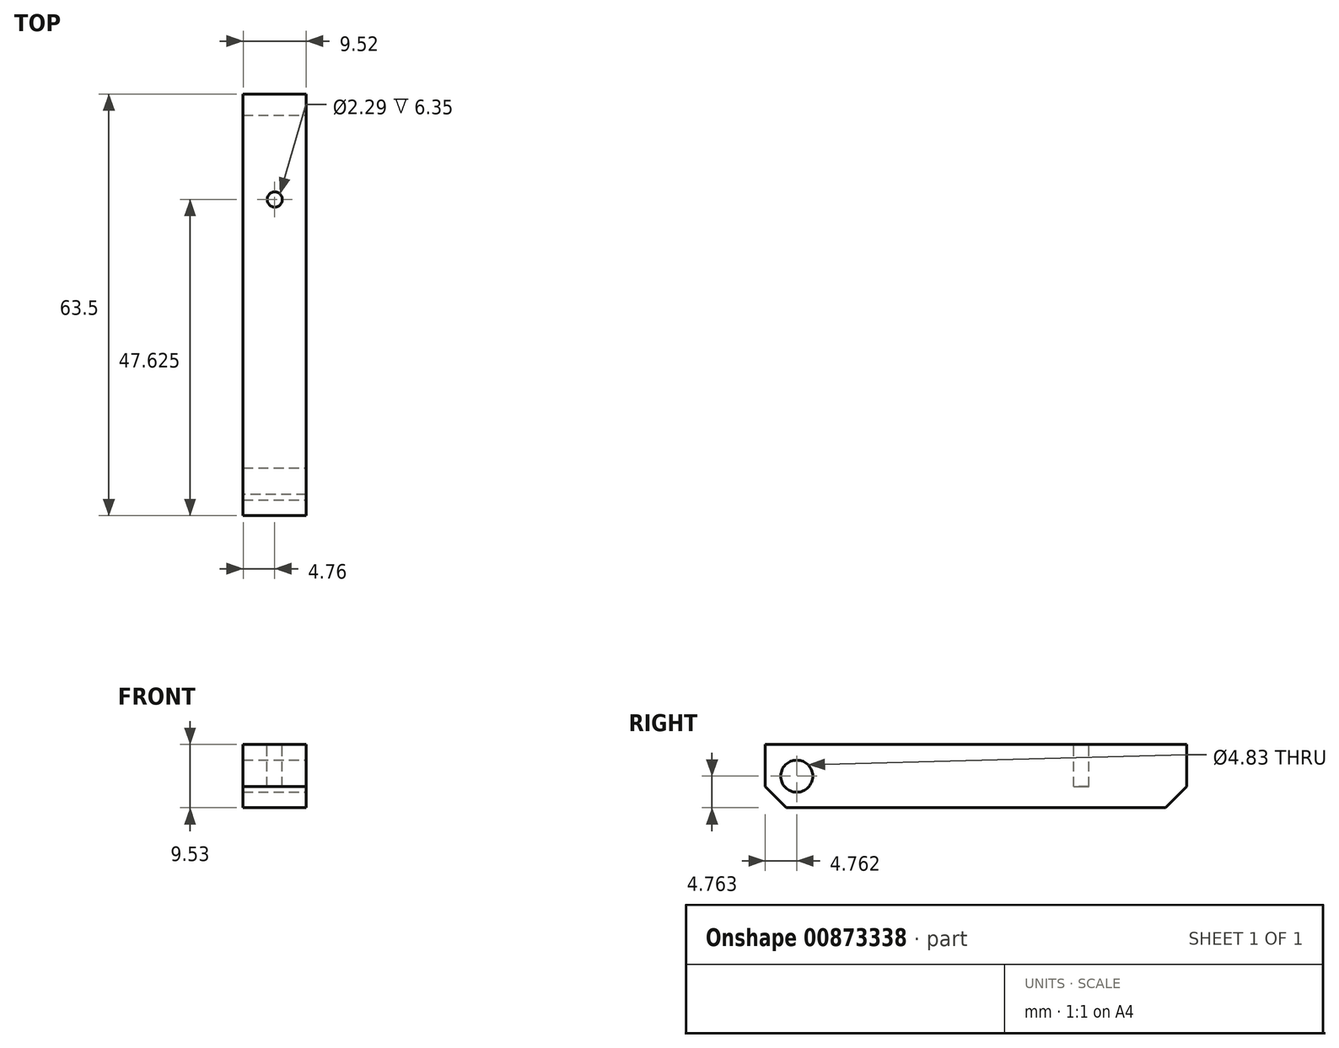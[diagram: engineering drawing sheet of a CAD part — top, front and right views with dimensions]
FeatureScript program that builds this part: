
annotation { "Feature Type Name" : "Feature", "Feature Type Description" : "" }
export const myFeature = defineFeature(function(context is Context, id is Id, definition is map)
    precondition{}
    {
        {
            var Q0;
            Q0=qCreatedBy(makeId("Top.planeOp"),FACE);
            var sketch = newSketch(context, id + "F0", { "sketchPlane" : qUnion([Q0])});
            skLineSegment(sketch, "E0.bottom", {"start": v(4.76, 31.75) * mm, "end": v(-4.76, 31.75) * mm});
            skLineSegment(sketch, "E0.top", {"start": v(4.76, -31.75) * mm, "end": v(-4.76, -31.75) * mm});
            skLineSegment(sketch, "E0.left", {"start": v(4.76, 31.75) * mm, "end": v(4.76, -31.75) * mm});
            skLineSegment(sketch, "E0.right", {"start": v(-4.76, 31.75) * mm, "end": v(-4.76, -31.75) * mm});
            skPoint(sketch, "E0.middle", {"position": v(0, 0) * mm});
            skSolve(sketch);
        }
        {
            var Q0;
            Q0=makeQuery(id+"F0.imprint","IMPRINT",FACE,{"disambiguationData":[TD([[makeQuery(id+"F0.imprint","IMPRINT",EDGE,{"derivedFrom":sQuery(id+"F0.wireOp",EDGE,"E0.bottom")}),1.0]])]});
            extrude(context, id + "F1", {"entities" : qUnion([Q0]), "depth" : 9.52 * mm, "offsetDistance" : 25.4 * mm});
        }
        {
            var Q0;
            Q0=makeQuery(id+"F1.opExtrude","SWEPT_FACE",FACE,{"disambiguationData":[OSD([sQuery(id+"F0.wireOp",EDGE,"E0.left")])]});
            var sketch = newSketch(context, id + "F2", { "sketchPlane" : qUnion([Q0])});
            skCircle(sketch, "E1", {"center": v(-26.99, 4.76) * mm, "radius": 2.41 * mm});
            skSolve(sketch);
        }
        {
            var Q0;
            Q0=makeQuery(id+"F2.imprint","IMPRINT",FACE,{"disambiguationData":[TD([[makeQuery(id+"F2.imprint","IMPRINT",EDGE,{"derivedFrom":sQuery(id+"F2.wireOp",EDGE,"E1")}),1.0]])]});
            extrude(context, id + "F3", {"entities" : qUnion([Q0]), "operationType" : NewBodyOperationType.REMOVE, "endBound" : BoundingType.THROUGH_ALL, "oppositeDirection" : true, "depth" : 25.4 * mm, "offsetDistance" : 25.4 * mm});
        }
        {
            var Q0;
            Q0=makeQuery(id+"F1.opExtrude","CAP_FACE",FACE,{"disambiguationData":[OSD([sQuery(id+"F0.wireOp",EDGE,"E0.bottom"),sQuery(id+"F0.wireOp",EDGE,"E0.top"),sQuery(id+"F0.wireOp",EDGE,"E0.left"),sQuery(id+"F0.wireOp",EDGE,"E0.right")])],"isStart":false});
            var sketch = newSketch(context, id + "F4", { "sketchPlane" : qUnion([Q0])});
            skCircle(sketch, "E2", {"center": v(0, 15.88) * mm, "radius": 1.14 * mm});
            skSolve(sketch);
        }
        {
            var Q0;
            Q0=makeQuery(id+"F4.imprint","IMPRINT",FACE,{"disambiguationData":[TD([[makeQuery(id+"F4.imprint","IMPRINT",EDGE,{"derivedFrom":sQuery(id+"F4.wireOp",EDGE,"E2")}),1.0]])]});
            extrude(context, id + "F5", {"entities" : qUnion([Q0]), "operationType" : NewBodyOperationType.REMOVE, "oppositeDirection" : true, "depth" : 6.35 * mm, "offsetDistance" : 25.4 * mm});
        }
        {
            var Q0;
            Q0=makeQuery(id+"F1.opExtrude","CAP_EDGE",EDGE,{"disambiguationData":[OSD([sQuery(id+"F0.wireOp",EDGE,"E0.top")])],"isStart":true});
            var Q1;
            Q1=makeQuery(id+"F1.opExtrude","CAP_EDGE",EDGE,{"disambiguationData":[OSD([sQuery(id+"F0.wireOp",EDGE,"E0.bottom")])],"isStart":true});
            chamfer(context, id + "F6", {"entities" : qUnion([Q0, Q1]), "width" : 3.17 * mm, "tangentPropagation" : true});
        }
    });
